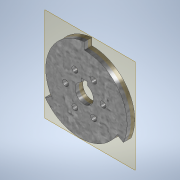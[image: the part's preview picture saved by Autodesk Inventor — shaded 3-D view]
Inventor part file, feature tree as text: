
AUTODESK INVENTOR PART (.ipt)
format: ipt  version: 2022 (Build 260153000, 153)  size: 224,256 bytes
history: native  units: in
note: dims shown in document units (in); Inventor stores cm internally (conversion verified against a paired STEP export)
features: sketch x2, extrude x2, pattern_circular x2, other x2, plane x1, thicken_offset x1, hole x1
ambient origin geometry x8: Origin, YZ Plane, XZ Plane, XY Plane, X Axis, Y Axis, Z Axis, Center Point
bodies: Solid1 (feature_tree)
feature tree (11):
  sketch  "Sketch1"  dims[d0=2.9528in d1=120.0deg]
  extrude  "Extrusion1"  TaperAngle=120.0deg  [1 undecoded]
  extrude  "Extrusion2"  Depth=0.25in TaperAngle=0.0deg
  pattern_circular  "Circular Pattern1"  Count=3 Angle=360.0deg
  plane  "Work Plane1"
  thicken_offset  "Thicken1"
  other  "A-Side Definition"
  hole  "Hole2"  [1 undecoded]
  pattern_circular  "Circular Pattern3"  [2 undecoded]
  sketch  "Sketch3"  dims[d2=0.2362in d3=0.25in d4=0.0in d5=1.1811in d6=360.0deg d8=0.5906in d20=0.1969in d21=0.1969in d22=0.25in d23=0.0in d24=0.005in d25=0.005in d26=0.6266in d27=0.3133in d28=0.1969in d29=0.75in d30=0.375in d31=0.25in d32=0.5635in d33=0.25in d34=0.0in d35=2.3622in d36=360.0deg]
  other  "Definition1"
note: 4 required parameter values undecoded (feature->parameter linkage not recoverable at this tier; creation-order binding heuristic only, values carry confidence <= 0.55)
